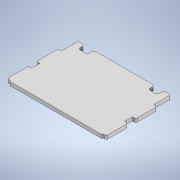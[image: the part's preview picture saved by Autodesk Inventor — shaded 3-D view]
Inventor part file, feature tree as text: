
AUTODESK INVENTOR PART (.ipt)
format: ipt  version: 2020 (Build 240168000, 168)  size: 180,736 bytes
history: native  units: mm
features: extrude x1, sketch x1
ambient origin geometry x8: Origin, YZ Plane, XZ Plane, XY Plane, X Axis, Y Axis, Z Axis, Center Point
bodies: Solid1 (feature_tree)
feature tree (2):
  extrude  "Extrusion1"  Depth=2.0mm
  sketch  "Sketch1"  dims[d3=4.5mm d8=2.0mm d11=2.0mm d12=2.0mm d13=9.0mm d14=83.0mm d15=12.7mm d16=12.7mm d17=2.0mm d18=3.0mm d19=3.0mm d20=135.5mm d23=94.00005mm d24=4.5mm d25=1.0mm d26=1.0mm d27=5.0mm d28=0.0mm d29=29.0mm d30=23.325mm d31=2.0mm d32=69.0mm d33=11.0mm d34=2.0mm]
